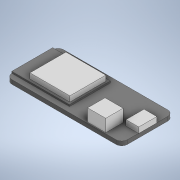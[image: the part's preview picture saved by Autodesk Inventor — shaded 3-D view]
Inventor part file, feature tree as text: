
AUTODESK INVENTOR PART (.ipt)
format: ipt  version: 2020 (Build 240168000, 168)  size: 166,400 bytes
history: native  units: in
note: dims shown in document units (in); Inventor stores cm internally (conversion verified against a paired STEP export)
features: extrude x6, other x1, fillet x1
ambient origin geometry x8: Origin, YZ Plane, XZ Plane, XY Plane, X Axis, Y Axis, Z Axis, Center Point
bodies: Solid1 (feature_tree)
feature tree (8):
  other  "ESP32 Feather"
  extrude  "PCB"  Depth=2.0079in
  fillet  "Fillet1"  Radius=0.0709in
  extrude  "ESP32PCB"  Depth=0.0295in
  extrude  "ESP32Shied"  Depth=1.0039in
  extrude  "Battery Connector"  Depth=0.6949in
  extrude  "Extrusion5"  Depth=0.0925in
  extrude  "Extrusion6"  Depth=0.9685in
